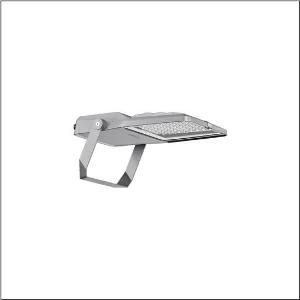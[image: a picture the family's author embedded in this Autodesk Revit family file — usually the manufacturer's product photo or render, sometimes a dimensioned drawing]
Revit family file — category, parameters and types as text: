
# Revit family: floodlight_fl_21_iq_mini___pl64_5xa7772b1e1a_f8ab
name_source: partatom
category: Lighting Fixtures
units: mm (PartAtom-declared; Revit-internal decimal feet)

## family parameters
Cut with Voids When Loaded = No
Host = Face
Light Source = No
Part Type = Normal
Room Calculation Point = No
Round Connector Dimension = Use Diameter
Shared = No

## types (1)
- --- (1 x LED, 4990 lm, 45.5 W, 2200K)
    Apparent Load = 46 VA
    CIE Flux Codes = 28 80 98 100 100
    Color Rendering = 70
    Color Temperature = 2200K
    Default Elevation = 1800 mm
    Description = Floodlight FL 21 iQ mini, floodlight, primary light control with lens, of PMMA, primary optical cover: protective disc, of toughened safety glass, transparent, light distribution: PL64, light emission: direct distribution, installation type: surface-mounted, LED, High Power LED, rated luminous flux: 4.990lm, luminous efficacy: 110lm/W, light colour: 722, colour temperature: 2200K, control: Street-Remote, Auto-Match, Temp-Guard, Night-Set, Smart-Wire, Desk-Remote (wireless, voltage-free reading and setting of iQ features in the workshop via application-optimized NFC function/RFID function), optimised constant luminous flux control (CLO 2.0), with terminal, 6-pole, mains connection: 220..240V, AC, 50/60Hz, start of lifetime: 46W, end of service life: 48W, reduction: 21W, luminaire housing, of diecast aluminium, powder-coated, Siteco® metallic grey (DB 702S), corrosivity category C5 mid according to DIN EN ISO 12944, sealing non-destructively replaceable, mounting bracket, of steel, galvanised, powder-coated, Siteco® metallic grey (DB 702S), protection rating (complete): IP66, insulation class (complete): insulation class II (safety insulation), certification: CE, ENEC, VDE, protection symbol: D, impact resistance: IK08, permissible operating ambient temperature: -40..+40°C, permissible operating ambient temperature for outdoor applications: -40..+50°C, standard: DIN EN 12944, LABS conformity tested according to VDMA 24364:2018-05, packaging unit: 1 piece

Light Distribution: PL64
    Height = 70 mm
    Lamp = 1 x LED
    Lamp Light Flux = 4990 lm
    Lamp Power = 45.5 W
    Lamp count = 1
    Length = 485 mm
    Luminous efficacy = 110 lm/W
    Manufacturer = Siteco
    ModVariant = No
    Model = 5XA7772B1E1A
    Number of Poles = 1
    OnlyDefault = Yes
    Power Factor = 1
    Product Name = Floodlight FL 21 iQ mini | PL64
    Product group = floodlight | pylon annexe
    ProductGroupID = 6200
    Protection Class = Protection class II
    Protection Degree = IP 66
    RLX_Detail_Level = 1
    RLX_Emergency_Light_Flux = 0 lm
    RLX_Emergency_Type = 0
    RLX_Emergency_Type_DB = No
    RlxData = <blob elided: 96109 chars, md5=c5d3d032>
    Socket = socket
    Standby Power = 0 W
    System Light Flux = 4990 lm
    System Power = 46 W
    Type Comments = factory setting: luminous flux: 100 % | dim-lin: 254 | 463 mA
    Type Image = l_1006845.jpg
    URL = http://relux.com
    VarID = @adj_117161
    Voltage = 0 V
    Weight = 0.00 kg
    Width = 337 mm

## geometry (parser evidence)
native form markers: Blend x4, Sweep x13
no freeform markers — native parametric forms only
